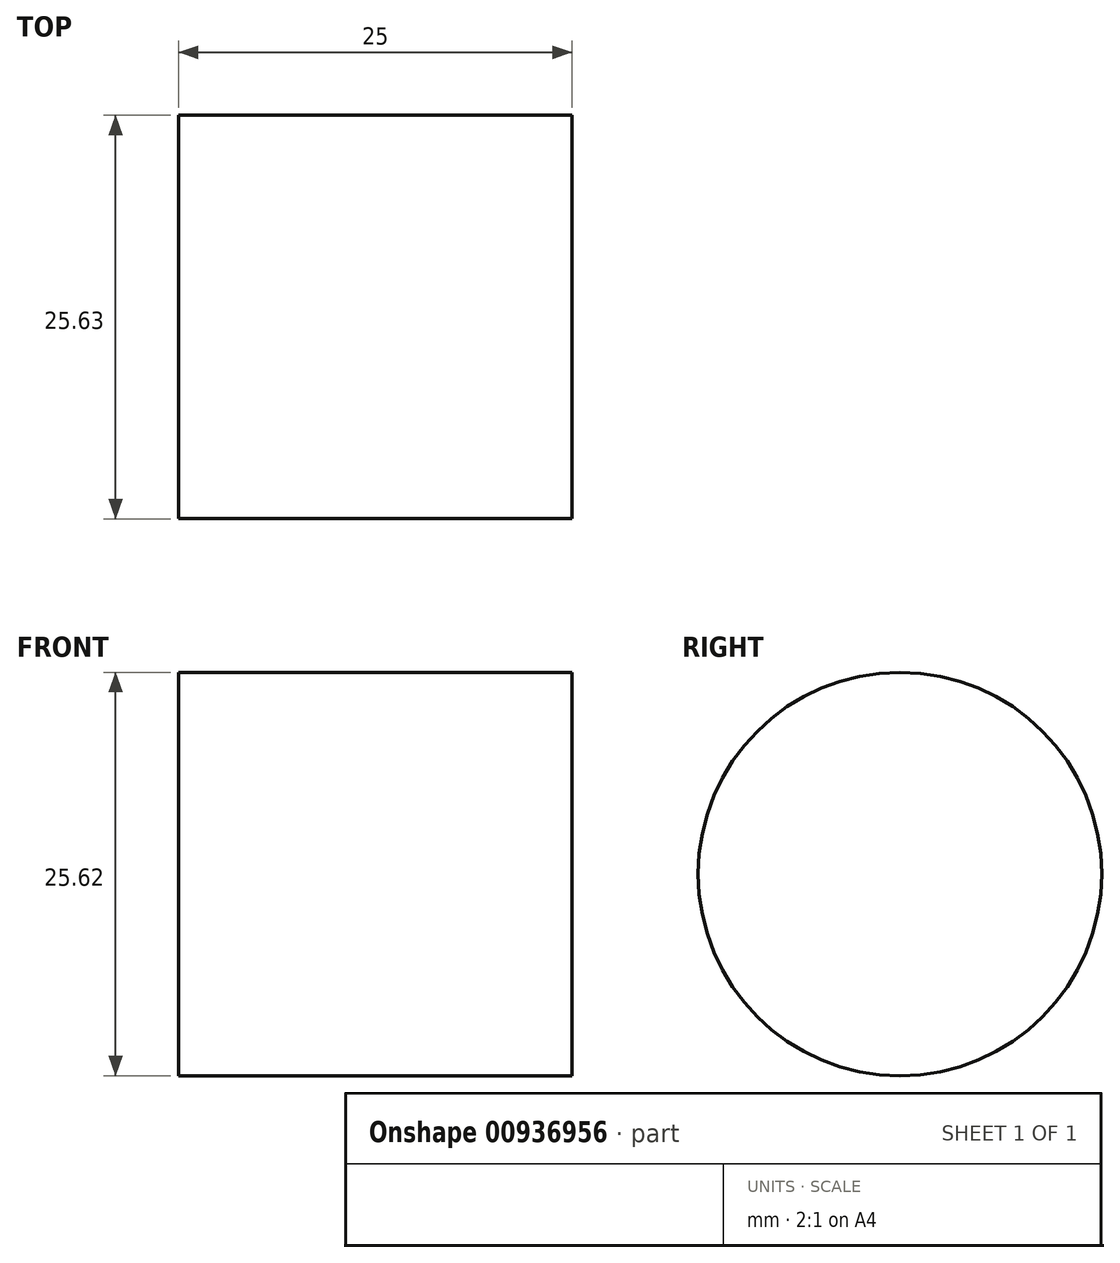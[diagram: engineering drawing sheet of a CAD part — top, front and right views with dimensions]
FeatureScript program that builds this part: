
annotation { "Feature Type Name" : "Feature", "Feature Type Description" : "" }
export const myFeature = defineFeature(function(context is Context, id is Id, definition is map)
    precondition{}
    {
        {
            var Q0;
            Q0=qCreatedBy(makeId("Right.planeOp"),FACE);
            var sketch = newSketch(context, id + "F0", { "sketchPlane" : qUnion([Q0])});
            skCircle(sketch, "E0", {"center": v(2.02, 0) * mm, "radius": 10 * mm});
            skSolve(sketch);
        }
        {
            var Q0;
            Q0=makeQuery(id+"F0.imprint","IMPRINT",FACE,{"disambiguationData":[TD([[makeQuery(id+"F0.imprint","IMPRINT",EDGE,{"derivedFrom":sQuery(id+"F0.wireOp",EDGE,"E0")}),1.0]])]});
            var sketch = newSketch(context, id + "F1", { "sketchPlane" : qUnion([Q0])});
            skCircle(sketch, "E1", {"center": v(2.27, 0) * mm, "radius": 12.81 * mm});
            skSolve(sketch);
        }
        {
            var Q0;
            Q0=makeQuery(id+"F1.imprint","IMPRINT",FACE,{"disambiguationData":[TD([[makeQuery(id+"F1.imprint","IMPRINT",EDGE,{"derivedFrom":makeQuery(id+"F0.imprint","IMPRINT",EDGE,{"derivedFrom":sQuery(id+"F0.wireOp",EDGE,"E0")})}),1.0]])]});
            var Q1;
            Q1=makeQuery(id+"F1.imprint","IMPRINT",FACE,{"disambiguationData":[TD([[makeQuery(id+"F1.imprint","IMPRINT",EDGE,{"derivedFrom":sQuery(id+"F1.wireOp",EDGE,"E1")}),1.0]])]});
            extrude(context, id + "F2", {"entities" : qUnion([Q0, Q1]), "depth" : 25 * mm, "offsetDistance" : 25 * mm});
        }
        {
            var Q0;
            Q0=sQuery(id+"F0.wireOp",EDGE,"E0");
            extrude(context, id + "F3", {"bodyType" : ToolBodyType.SURFACE, "surfaceEntities" : qUnion([Q0]), "oppositeDirection" : true, "depth" : 9.7 * mm, "offsetDistance" : 25 * mm});
        }
    });
